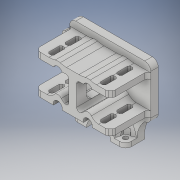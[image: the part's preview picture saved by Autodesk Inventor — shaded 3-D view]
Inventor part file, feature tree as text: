
AUTODESK INVENTOR PART (.ipt)
format: ipt  version: 2018 (Build 220112000, 112)  size: 865,280 bytes
history: native  units: in
note: dims shown in document units (in); Inventor stores cm internally (conversion verified against a paired STEP export)
features: sketch x21, extrude x20, projected_geometry x10, fillet x7, chamfer x4, mirror x2, plane x1, emboss x1
ambient origin geometry x8: Origin, YZ Plane, XZ Plane, XY Plane, X Axis, Y Axis, Z Axis, Center Point
bodies: Solid1 (feature_tree)
feature tree (66):
  extrude  "Extrusion1"  Depth=0.1969in TaperAngle=0.0deg
  extrude  "Extrusion2"  Depth=0.7874in
  fillet  "Fillet1"  Radius=0.126in
  extrude  "Extrusion3"  Depth=0.1575in
  extrude  "Extrusion4"  Depth=0.3937in
  extrude  "Extrusion5"  Depth=0.1969in TaperAngle=0.0deg
  extrude  "Extrusion6"  Depth=0.1496in TaperAngle=0.0deg
  extrude  "Extrusion7"  Depth=0.0394in TaperAngle=0.0deg
  extrude  "Extrusion8"  Depth=0.1575in TaperAngle=0.0deg
  chamfer  "Chamfer1"  Distance=0.1575in
  fillet  "Fillet2"  Radius=0.1575in
  fillet  "Fillet3"  Radius=0.1575in
  extrude  "Extrusion10"  Depth=0.1575in
  extrude  "Extrusion16"  Depth=0.1575in
  mirror  "Mirror3"
  extrude  "Extrusion17"  Depth=0.1575in TaperAngle=0.0deg
  extrude  "Extrusion18"  Depth=0.7874in
  fillet  "Fillet8"  Radius=0.2244in
  extrude  "Extrusion19"  Depth=0.3937in TaperAngle=0.0deg
  fillet  "Fillet9"  Radius=0.2756in
  extrude  "Extrusion21"  TaperAngle=0.0deg  [1 undecoded]
  extrude  "Extrusion23"  Depth=0.2559in
  plane  "Work Plane1"
  extrude  "Extrusion25"  Depth=0.3937in TaperAngle=0.0deg
  extrude  "Extrusion27"  Depth=0.0787in
  extrude  "Extrusion28"  Depth=0.2362in
  chamfer  "Chamfer12"  Distance=0.689in
  mirror  "Mirror5"
  extrude  "Extrusion29"  Depth=0.0787in
  extrude  "Extrusion30"  Depth=0.1575in
  chamfer  "Chamfer14"  Distance=1.9685in
  chamfer  "Chamfer15"  Distance=0.1575in
  fillet  "Fillet10"  Radius=0.7126in
  emboss  "Emboss1"
  fillet  "Fillet11"  Radius=0.9843in
  sketch  "Sketch1"  dims[d0=2.126in d2=0.1969in d3=0.0in]
  sketch  "Sketch2"  dims[d4=0.7874in d5=0.7874in d6=0.126in]
  sketch  "Sketch3"  dims[d7=0.1969in d8=0.0in d9=0.1575in]
  sketch  "Sketch4"  dims[d10=1.1811in d12=0.3937in]
  sketch  "Sketch5"  dims[d13=0.6339in d14=0.1969in d15=0.0in]
  projected_geometry  "Projected Loop1"
  sketch  "Sketch6"  dims[d16=0.4843in d17=0.1496in d18=0.0709in d19=0.0in d20=0.0in]
  sketch  "Sketch9"  dims[d21=0.1181in d22=0.0394in d23=0.0in]
  projected_geometry  "Projected Loop2"
  projected_geometry  "Projected Loop3"
  sketch  "Sketch10"  dims[d24=0.1181in d25=0.1575in d26=0.0in d29=0.1575in d30=0.0in d31=0.1575in d32=0.0in]
  projected_geometry  "Projected Loop4"
  sketch  "Sketch13"  dims[d33=0.1969in d34=0.0787in d35=45.0deg d43=0.1575in]
  sketch  "Sketch20"  dims[d44=0.1575in d45=0.126in]
  projected_geometry  "Projected Loop7"
  sketch  "Sketch21"  dims[d46=0.1575in d47=0.1575in]
  sketch  "Sketch22"  dims[d48=0.1575in d49=0.1575in d50=0.0in]
  projected_geometry  "Projected Loop8"
  sketch  "Sketch23"  dims[d69=0.7874in d70=0.5906in d138=0.2244in]
  sketch  "Sketch26"  dims[d139=0.252in d140=0.3937in d141=0.0in d142=0.2756in]
  sketch  "Sketch28"  dims[d143=0.5118in d144=0.0in d145=0.0in]
  sketch  "Sketch31"  dims[d146=0.0906in d147=0.2559in]
  projected_geometry  "Projected Loop10"
  sketch  "Sketch34"  dims[d148=0.2008in d149=0.3937in d150=0.0in]
  projected_geometry  "Projected Loop11"
  sketch  "Sketch35"  dims[d151=0.0787in d153=0.0787in]
  sketch  "Sketch37"  dims[d154=0.0787in d155=0.0in d164=0.2362in]
  projected_geometry  "Projected Loop12"
  sketch  "Sketch38"  dims[d165=0.0787in]
  projected_geometry  "Projected Loop13"
  sketch  "Sketch39"  dims[d181=0.0335in d183=0.689in d194=0.189in d195=0.1575in d196=1.9685in d197=0.1575in d198=0.7126in d206=0.9843in d207=0.0in d216=0.2362in d217=1.1811in d218=0.0in d227=0.1457in d228=0.1181in d229=0.2362in d230=0.2559in d231=0.3937in d232=0.0in d243=0.4724in d244=0.6299in d245=0.6299in d246=0.2362in d247=0.3937in d248=0.0in d249=0.1378in d250=0.3543in d251=0.3543in d252=0.0787in d255=0.1181in d256=0.2362in d257=0.3937in d258=0.0in d259=0.0394in d260=0.0787in d261=45.0deg d265=0.3937in d266=0.0in d267=0.2559in d268=135.0deg d269=0.315in d270=135.0deg d271=0.4331in d272=0.6299in d273=0.3937in d274=0.0in d275=0.0394in d276=0.0787in d277=45.0deg d278=0.0945in d279=0.0787in d280=45.0deg d281=0.0787in d282=1.378in d283=0.0in d284=0.1575in d285=0.1181in d286=0.4921in d287=0.0394in d288=0.0in d289=0.0787in]
note: 1 required parameter value undecoded (feature->parameter linkage not recoverable at this tier; creation-order binding heuristic only, values carry confidence <= 0.55)
